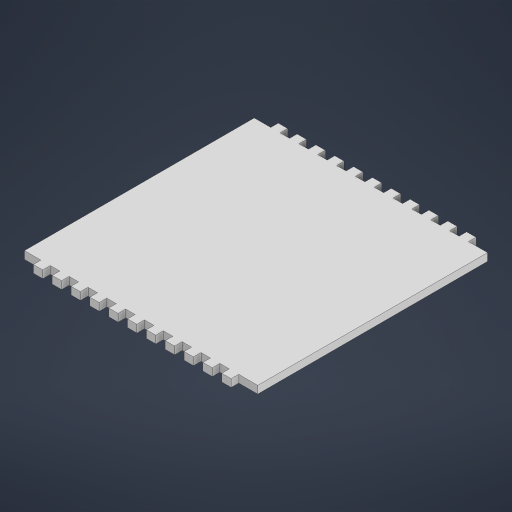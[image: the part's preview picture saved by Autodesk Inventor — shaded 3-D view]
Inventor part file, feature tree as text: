
AUTODESK INVENTOR PART (.ipt)
format: ipt  version: 2023 (Build 270158030, 158C)  size: 245,760 bytes
history: native  units: mm
features: extrude x1, sketch x1
ambient origin geometry x8: Origin, YZ Plane, XZ Plane, XY Plane, X Axis, Y Axis, Z Axis, Center Point
bodies: Solid1 (feature_tree)
feature tree (2):
  extrude  "Extrusion1"  [1 undecoded]
  sketch  "Sketch1"  dims[d0=4.0mm d1=0.0mm]
note: 1 required parameter value undecoded (feature->parameter linkage not recoverable at this tier; creation-order binding heuristic only, values carry confidence <= 0.55)
